# Revit family: 304_AB__B___G_B_E-JUST3
name_source: partatom
category: Pipe Accessories
units: mm (PartAtom-declared; Revit-internal decimal feet)

## family parameters
Always vertical = Yes
Cut with Voids When Loaded = No
Part Type = Valve - Breaks Into
Round Connector Dimension = Use Diameter
Shared = No
Work Plane-Based = No

## types (2) — shared parameters
CAT0 = Yes
Description = E-Just - Dynamic Balancing valve - Adjusteble Cartridge
L1 = 34 mm
L1__ve = -34 mm
L2 = 101 mm
L2D = 169 mm
L2D_Min = 3048 mm  [stored 10 ft]
L4 = 25 mm  [stored 0.082021 ft]
L66 = 65 mm  [stored 0.213255 ft]
L66__ve = -65 mm  [stored -0.213255 ft]
L7 = 56 mm  [stored 0.183727 ft]
LA = 31 mm  [stored 0.101706 ft]
LL = 85 mm
Manufacturer = FlowCon
QmdConnectorList = 301;D;302;D
R33 = 6 mm  [stored 0.019685 ft]
RA = 11 mm  [stored 0.0360892 ft]
URL = http://flowcon.com
magiPartTypeId = 304
magiProductFamilyId = AB*.B.*.G.B.E-JUST3
zero-valued in all types: MC_Default_elevation

## per-type parameters (varying)
| type | CenSd_RN_6 | CenSd_SW_6 | D | H11 | H12 | L5 | L6 | L6__ve | R1 | R2 | R3 | RN | SW | W2D |
| AB40.B.*.G.B.E-JUST3 | 18 mm | 25 mm  [stored 0.082021 ft] | 40 mm | 42 mm | 59 mm | 34 mm | 68 mm | -68 mm | 22 mm  [stored 0.0721785 ft] | 26 mm | 29 mm | 21 mm | 29 mm | 40 mm  [stored 0.131234 ft] |
| AB50.B.*.G.B.E-JUST3 | 22 mm  [stored 0.0721785 ft] | 31 mm  [stored 0.101706 ft] | 50 mm | 38 mm | 57 mm | 33 mm | 66 mm | -66 mm | 27 mm  [stored 0.0885827 ft] | 32 mm | 36 mm  [stored 0.11811 ft] | 26 mm | 36 mm  [stored 0.11811 ft] | 50 mm  [stored 0.164042 ft] |

note: column(s) folded — value = type name in every type: magiProductCode, magiProductId

note: [stored X ft] marks values corroborated as IEEE doubles in the binary element streams (Revit-internal decimal feet)

## geometry (parser evidence)
native form markers: Sweep x1
no freeform markers — native parametric forms only
